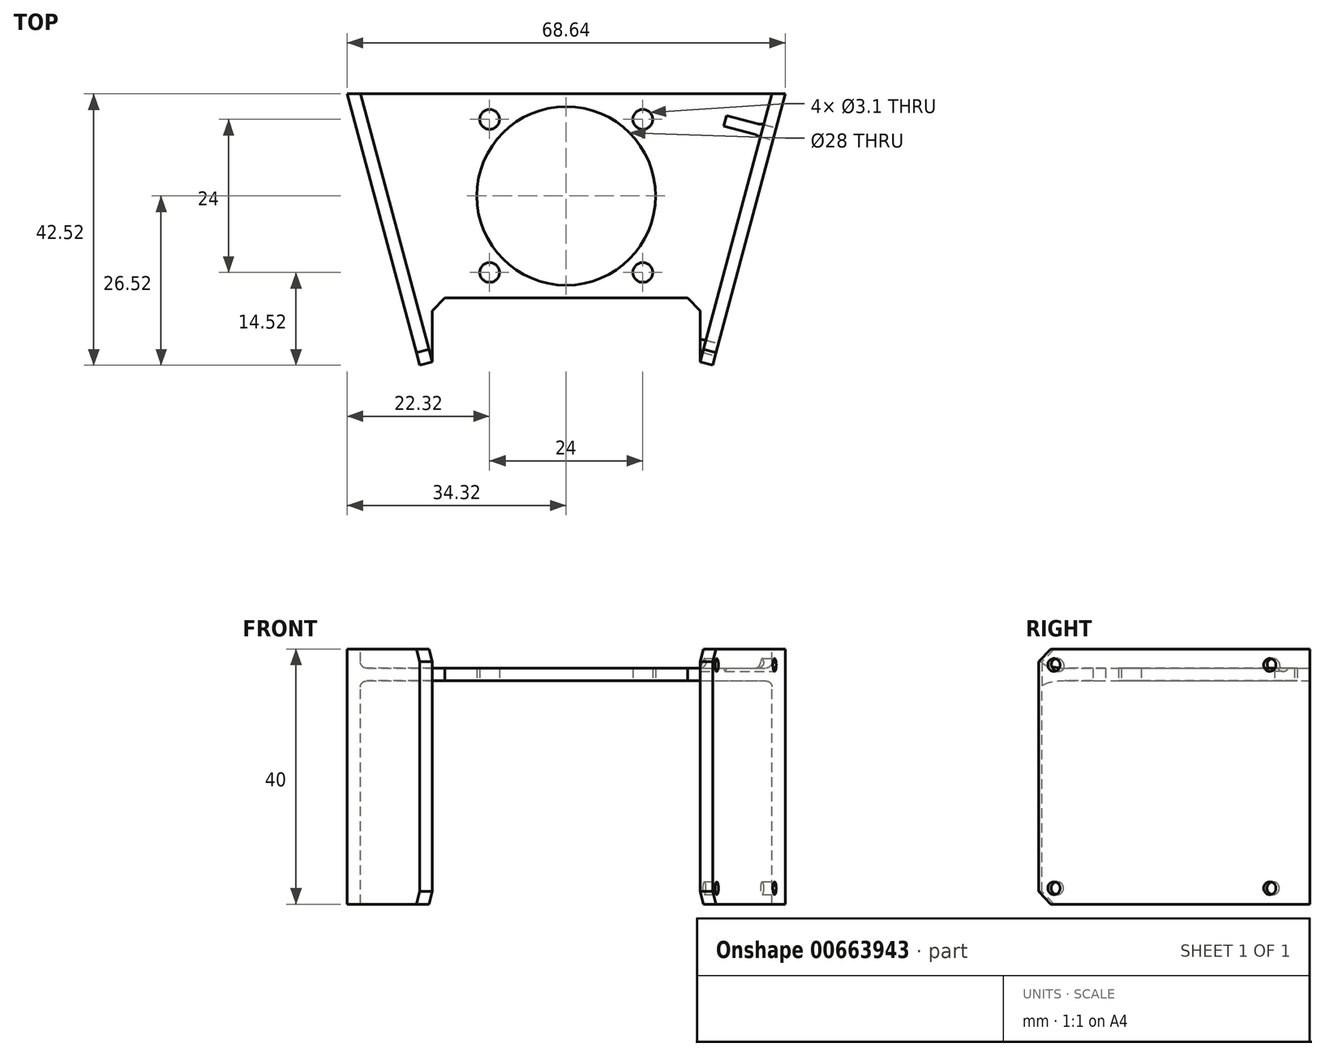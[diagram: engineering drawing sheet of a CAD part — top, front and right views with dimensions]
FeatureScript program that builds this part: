
annotation { "Feature Type Name" : "Feature", "Feature Type Description" : "" }
export const myFeature = defineFeature(function(context is Context, id is Id, definition is map)
    precondition{}
    {
        {
            var Q0;
            Q0=qCreatedBy(makeId("Top.planeOp"),FACE);
            var sketch = newSketch(context, id + "F0", { "sketchPlane" : qUnion([Q0])});
            skLineSegment(sketch, "E0.bottom", {"start": v(-16, 16) * mm, "end": v(16, 16) * mm});
            skLineSegment(sketch, "E0.top", {"start": v(-16, -16) * mm, "end": v(16, -16) * mm});
            skLineSegment(sketch, "E0.left", {"start": v(-16, 16) * mm, "end": v(-16, -16) * mm});
            skLineSegment(sketch, "E0.right", {"start": v(16, 16) * mm, "end": v(16, -16) * mm});
            skPoint(sketch, "E1.end.orphan", {"position": v(-27.25, 16) * mm});
            skPoint(sketch, "E2.end.orphan", {"position": v(-16, -26) * mm});
            skLineSegment(sketch, "E3", {"start": v(-16, -16) * mm, "end": v(-21, -16) * mm});
            skLineSegment(sketch, "E4", {"start": v(-21, -16) * mm, "end": v(-21, -26) * mm});
            skLineSegment(sketch, "E5", {"start": v(-32.25, 16) * mm, "end": v(-16, 16) * mm});
            skLineSegment(sketch, "E6", {"start": v(-21, -26) * mm, "end": v(-22.93, -26.52) * mm});
            skLineSegment(sketch, "E7", {"start": v(-22.93, -26.52) * mm, "end": v(-34.19, 15.48) * mm});
            skLineSegment(sketch, "E8.MirrorCS", {"start": v(16, -16) * mm, "end": v(21, -16) * mm});
            skLineSegment(sketch, "E9.MirrorCS", {"start": v(21, -16) * mm, "end": v(21, -26) * mm});
            skLineSegment(sketch, "E10.MirrorCS", {"start": v(21, -26) * mm, "end": v(22.93, -26.52) * mm});
            skLineSegment(sketch, "E11.MirrorCS", {"start": v(22.93, -26.52) * mm, "end": v(34.19, 15.48) * mm});
            skLineSegment(sketch, "E12.MirrorCS", {"start": v(32.25, 16) * mm, "end": v(16, 16) * mm});
            skCircle(sketch, "E13", {"center": v(0, 0) * mm, "radius": 14 * mm});
            skCircle(sketch, "E14", {"center": v(-12, 12) * mm, "radius": 1.55 * mm});
            skCircle(sketch, "E15.0.1.0", {"center": v(-12, -12) * mm, "radius": 1.55 * mm});
            skCircle(sketch, "E15.1.0.0", {"center": v(12, 12) * mm, "radius": 1.55 * mm});
            skCircle(sketch, "E15.1.1.0", {"center": v(12, -12) * mm, "radius": 1.55 * mm});
            skLineSegment(sketch, "E15.direction1", {"start": v(-12, 12) * mm, "end": v(12, 12) * mm, "construction": true});
            skLineSegment(sketch, "E15.direction2", {"start": v(-12, 12) * mm, "end": v(-12, -12) * mm, "construction": true});
            skPoint(sketch, "E16.orphan", {"position": v(-34.32, 16) * mm});
            skPoint(sketch, "E17.MirrorCS.end.orphan", {"position": v(32.25, 16) * mm});
            skPoint(sketch, "E17.MirrorCS.start.orphan", {"position": v(34.32, 16) * mm});
            skLineSegment(sketch, "E18", {"start": v(-32.25, 16) * mm, "end": v(-34.32, 16) * mm});
            skLineSegment(sketch, "E19", {"start": v(-34.32, 16) * mm, "end": v(-34.19, 15.48) * mm});
            skLineSegment(sketch, "E20.MirrorCS", {"start": v(32.25, 16) * mm, "end": v(34.32, 16) * mm});
            skLineSegment(sketch, "E21.MirrorCS", {"start": v(34.32, 16) * mm, "end": v(34.19, 15.48) * mm});
            skSolve(sketch);
        }
        {
            var Q0;
            Q0 = qSketchRegion(id + "F0", true);
            extrude(context, id + "F1", {"entities" : qUnion([Q0]), "depth" : 2 * mm, "offsetDistance" : 25 * mm});
        }
        {
            var Q0;
            Q0=makeQuery(id+"F1.opExtrude","CAP_FACE",FACE,{"disambiguationData":[OSD([sQuery(id+"F0.wireOp",EDGE,"E0.bottom"),sQuery(id+"F0.wireOp",EDGE,"E0.top"),sQuery(id+"F0.wireOp",EDGE,"E3"),sQuery(id+"F0.wireOp",EDGE,"E4"),sQuery(id+"F0.wireOp",EDGE,"E5"),sQuery(id+"F0.wireOp",EDGE,"E6"),sQuery(id+"F0.wireOp",EDGE,"E7"),sQuery(id+"F0.wireOp",EDGE,"E8.MirrorCS"),sQuery(id+"F0.wireOp",EDGE,"E9.MirrorCS"),sQuery(id+"F0.wireOp",EDGE,"E10.MirrorCS"),sQuery(id+"F0.wireOp",EDGE,"E11.MirrorCS"),sQuery(id+"F0.wireOp",EDGE,"E12.MirrorCS"),sQuery(id+"F0.wireOp",EDGE,"E13"),sQuery(id+"F0.wireOp",EDGE,"E14"),sQuery(id+"F0.wireOp",EDGE,"E15.0.1.0"),sQuery(id+"F0.wireOp",EDGE,"E15.1.0.0"),sQuery(id+"F0.wireOp",EDGE,"E15.1.1.0"),sQuery(id+"F0.wireOp",EDGE,"g3s6btQA-WjSZ-mLAz-3Mlx-ke06xdscXXFO"),sQuery(id+"F0.wireOp",EDGE,"cd634426-3a8a-407d-a25f-cc673fb204210.MirrorCS")])],"isStart":true});
            var sketch = newSketch(context, id + "F2", { "sketchPlane" : qUnion([Q0])});
            skLineSegment(sketch, "E22", {"start": v(21, 26) * mm, "end": v(21, 26) * mm});
            skLineSegment(sketch, "E23", {"start": v(22.93, 26.52) * mm, "end": v(22.93, 26.52) * mm});
            skLineSegment(sketch, "E24.MirrorCS", {"start": v(-21, 26) * mm, "end": v(-21, 26) * mm});
            skLineSegment(sketch, "E25.MirrorCS", {"start": v(-22.93, 26.52) * mm, "end": v(-22.93, 26.52) * mm});
            skPoint(sketch, "E26.MirrorCS.end.orphan", {"position": v(-22.93, 26.52) * mm});
            skPoint(sketch, "E26.MirrorCS.start.orphan", {"position": v(-21, 26) * mm});
            skLineSegment(sketch, "E27", {"start": v(-22.93, 26.52) * mm, "end": v(-21, 26) * mm});
            skLineSegment(sketch, "E28", {"start": v(-22.93, 26.52) * mm, "end": v(-34.32, -16) * mm});
            skLineSegment(sketch, "E29", {"start": v(-34.32, -16) * mm, "end": v(-32.25, -16) * mm});
            skLineSegment(sketch, "E30", {"start": v(-21, 26) * mm, "end": v(-32.25, -16) * mm});
            skLineSegment(sketch, "E31.MirrorCS", {"start": v(21, 26) * mm, "end": v(32.25, -16) * mm});
            skLineSegment(sketch, "E32.MirrorCS", {"start": v(22.93, 26.52) * mm, "end": v(21, 26) * mm});
            skLineSegment(sketch, "E33.MirrorCS", {"start": v(22.93, 26.52) * mm, "end": v(34.32, -16) * mm});
            skLineSegment(sketch, "E34.MirrorCS", {"start": v(34.32, -16) * mm, "end": v(32.25, -16) * mm});
            skSolve(sketch);
        }
        {
            var Q0;
            Q0 = qSketchRegion(id + "F2", true);
            extrude(context, id + "F3", {"entities" : qUnion([Q0]), "operationType" : NewBodyOperationType.ADD, "depth" : 35 * mm, "offsetDistance" : 25 * mm, "hasSecondDirection" : true, "secondDirectionOppositeDirection" : true, "secondDirectionDepth" : 5 * mm});
        }
        {
            var Q0;
            Q0=makeQuery(id+"F3.boolean.opBoolean","MERGE",FACE,{"derivedFrom":[makeQuery(id+"F1.opExtrude","SWEPT_FACE",FACE,{"disambiguationData":[OSD([sQuery(id+"F0.wireOp",EDGE,"E11.MirrorCS"),sQuery(id+"F0.wireOp",EDGE,"E21.MirrorCS")])]}),makeQuery(id+"F3.opExtrude","SWEPT_FACE",FACE,{"disambiguationData":[OSD([sQuery(id+"F2.wireOp",EDGE,"E33.MirrorCS")])]})]});
            var sketch = newSketch(context, id + "F4", { "sketchPlane" : qUnion([Q0])});
            skCircle(sketch, "E35", {"center": v(-17.18, 2.5) * mm, "radius": 1 * mm});
            skCircle(sketch, "E36.0.1.0", {"center": v(-17.18, -32.5) * mm, "radius": 1 * mm});
            skCircle(sketch, "E36.1.0.0", {"center": v(17.82, 2.5) * mm, "radius": 1 * mm});
            skCircle(sketch, "E36.1.1.0", {"center": v(17.82, -32.5) * mm, "radius": 1 * mm});
            skLineSegment(sketch, "E36.direction1", {"start": v(-17.18, 2.5) * mm, "end": v(17.82, 2.5) * mm, "construction": true});
            skLineSegment(sketch, "E36.direction2", {"start": v(-17.18, 2.5) * mm, "end": v(-17.18, -32.5) * mm, "construction": true});
            skSolve(sketch);
        }
        {
            var Q0;
            Q0 = qSketchRegion(id + "F4", true);
            extrude(context, id + "F5", {"entities" : qUnion([Q0]), "operationType" : NewBodyOperationType.REMOVE, "oppositeDirection" : true, "depth" : 8 * mm, "offsetDistance" : 25 * mm});
        }
        {
            var Q0;
            Q0=makeQuery(id+"F3.opExtrude","CAP_EDGE",EDGE,{"disambiguationData":[OSD([sQuery(id+"F2.wireOp",EDGE,"E32.MirrorCS")])],"isStart":false});
            var Q1;
            Q1=makeQuery(id+"F3.opExtrude","CAP_EDGE",EDGE,{"disambiguationData":[OSD([sQuery(id+"F2.wireOp",EDGE,"E32.MirrorCS")])],"isStart":true});
            var Q2;
            Q2=makeQuery(id+"F3.opExtrude","CAP_EDGE",EDGE,{"disambiguationData":[OSD([sQuery(id+"F2.wireOp",EDGE,"E27")])],"isStart":true});
            var Q3;
            Q3=makeQuery(id+"F3.opExtrude","CAP_EDGE",EDGE,{"disambiguationData":[OSD([sQuery(id+"F2.wireOp",EDGE,"E27")])],"isStart":false});
            var Q4;
            Q4=makeQuery(id+"F1.opExtrude","SWEPT_EDGE",EDGE,{"disambiguationData":[OSD([sQuery(id+"F0.wireOp",EDGE,"E3"),sQuery(id+"F0.wireOp",EDGE,"E4")])]});
            var Q5;
            Q5=makeQuery(id+"F1.opExtrude","SWEPT_EDGE",EDGE,{"disambiguationData":[OSD([sQuery(id+"F0.wireOp",EDGE,"E8.MirrorCS"),sQuery(id+"F0.wireOp",EDGE,"E9.MirrorCS")])]});
            chamfer(context, id + "F6", {"entities" : qUnion([Q0, Q1, Q2, Q3, Q4, Q5]), "width" : 2 * mm, "tangentPropagation" : true});
        }
        {
            var Q0;
            {var subQ0=makeQuery(id+"F1.opExtrude","CAP_FACE",FACE,{"disambiguationData":[OSD([sQuery(id+"F0.wireOp",EDGE,"E0.bottom"),sQuery(id+"F0.wireOp",EDGE,"E0.top"),sQuery(id+"F0.wireOp",EDGE,"E3"),sQuery(id+"F0.wireOp",EDGE,"E4"),sQuery(id+"F0.wireOp",EDGE,"E5"),sQuery(id+"F0.wireOp",EDGE,"E6"),sQuery(id+"F0.wireOp",EDGE,"E7"),sQuery(id+"F0.wireOp",EDGE,"E8.MirrorCS"),sQuery(id+"F0.wireOp",EDGE,"E9.MirrorCS"),sQuery(id+"F0.wireOp",EDGE,"E10.MirrorCS"),sQuery(id+"F0.wireOp",EDGE,"E11.MirrorCS"),sQuery(id+"F0.wireOp",EDGE,"E12.MirrorCS"),sQuery(id+"F0.wireOp",EDGE,"E13"),sQuery(id+"F0.wireOp",EDGE,"E14"),sQuery(id+"F0.wireOp",EDGE,"E15.0.1.0"),sQuery(id+"F0.wireOp",EDGE,"E15.1.0.0"),sQuery(id+"F0.wireOp",EDGE,"E15.1.1.0"),sQuery(id+"F0.wireOp",EDGE,"E18"),sQuery(id+"F0.wireOp",EDGE,"E19"),sQuery(id+"F0.wireOp",EDGE,"E20.MirrorCS"),sQuery(id+"F0.wireOp",EDGE,"E21.MirrorCS")])],"isStart":false});var subQ1=makeQuery(id+"F3.opExtrude","SWEPT_FACE",FACE,{"disambiguationData":[OSD([sQuery(id+"F2.wireOp",EDGE,"E31.MirrorCS")])]});Q0=makeQuery(id+"F5.boolean.opBoolean","SPLIT",EDGE,{"disambiguationData":[TD([subQ0,subQ1,makeQuery(id+"F5.opExtrude","SWEPT_FACE",FACE,{"disambiguationData":[OSD([sQuery(id+"F4.wireOp",EDGE,"E35")])]}),makeQuery(id+"F5.opExtrude","SWEPT_FACE",FACE,{"disambiguationData":[OSD([sQuery(id+"F4.wireOp",EDGE,"E36.1.0.0")])]})])],"derivedFrom":makeQuery(id+"F3.boolean.opBoolean","INTERSECT",EDGE,{"derivedFrom":[subQ0,subQ1]})});}
            var Q1;
            {var subQ0=makeQuery(id+"F3.opExtrude","SWEPT_FACE",FACE,{"disambiguationData":[OSD([sQuery(id+"F2.wireOp",EDGE,"E31.MirrorCS")])]});var subQ1=sQuery(id+"F0.wireOp",EDGE,"E20.MirrorCS");var subQ2=sQuery(id+"F0.wireOp",EDGE,"E18");var subQ3=sQuery(id+"F0.wireOp",EDGE,"E12.MirrorCS");var subQ4=sQuery(id+"F0.wireOp",EDGE,"E5");var subQ5=sQuery(id+"F0.wireOp",EDGE,"E0.bottom");var subQ6=makeQuery(id+"F1.opExtrude","CAP_FACE",FACE,{"disambiguationData":[OSD([subQ5,sQuery(id+"F0.wireOp",EDGE,"E0.top"),sQuery(id+"F0.wireOp",EDGE,"E3"),sQuery(id+"F0.wireOp",EDGE,"E4"),subQ4,sQuery(id+"F0.wireOp",EDGE,"E6"),sQuery(id+"F0.wireOp",EDGE,"E7"),sQuery(id+"F0.wireOp",EDGE,"E8.MirrorCS"),sQuery(id+"F0.wireOp",EDGE,"E9.MirrorCS"),sQuery(id+"F0.wireOp",EDGE,"E10.MirrorCS"),sQuery(id+"F0.wireOp",EDGE,"E11.MirrorCS"),subQ3,sQuery(id+"F0.wireOp",EDGE,"E13"),sQuery(id+"F0.wireOp",EDGE,"E14"),sQuery(id+"F0.wireOp",EDGE,"E15.0.1.0"),sQuery(id+"F0.wireOp",EDGE,"E15.1.0.0"),sQuery(id+"F0.wireOp",EDGE,"E15.1.1.0"),subQ2,sQuery(id+"F0.wireOp",EDGE,"E19"),subQ1,sQuery(id+"F0.wireOp",EDGE,"E21.MirrorCS")])],"isStart":false});Q1=makeQuery(id+"F5.boolean.opBoolean","SPLIT",EDGE,{"disambiguationData":[TD([subQ6,makeQuery(id+"F1.opExtrude","SWEPT_FACE",FACE,{"disambiguationData":[OSD([subQ5,subQ4,subQ3,subQ2,subQ1])]}),makeQuery(id+"F3.opExtrude","SWEPT_FACE",FACE,{"disambiguationData":[OSD([sQuery(id+"F2.wireOp",EDGE,"E29")])]}),subQ0,makeQuery(id+"F3.opExtrude","SWEPT_FACE",FACE,{"disambiguationData":[OSD([sQuery(id+"F2.wireOp",EDGE,"E34.MirrorCS")])]}),makeQuery(id+"F5.opExtrude","SWEPT_FACE",FACE,{"disambiguationData":[OSD([sQuery(id+"F4.wireOp",EDGE,"E36.1.0.0")])]})])],"derivedFrom":makeQuery(id+"F3.boolean.opBoolean","INTERSECT",EDGE,{"derivedFrom":[subQ6,subQ0]})});}
            var Q2;
            {var subQ0=makeQuery(id+"F3.opExtrude","SWEPT_FACE",FACE,{"disambiguationData":[OSD([sQuery(id+"F2.wireOp",EDGE,"E31.MirrorCS")])]});var subQ1=sQuery(id+"F0.wireOp",EDGE,"E9.MirrorCS");var subQ2=sQuery(id+"F0.wireOp",EDGE,"E10.MirrorCS");var subQ3=makeQuery(id+"F1.opExtrude","CAP_FACE",FACE,{"disambiguationData":[OSD([sQuery(id+"F0.wireOp",EDGE,"E0.bottom"),sQuery(id+"F0.wireOp",EDGE,"E0.top"),sQuery(id+"F0.wireOp",EDGE,"E3"),sQuery(id+"F0.wireOp",EDGE,"E4"),sQuery(id+"F0.wireOp",EDGE,"E5"),sQuery(id+"F0.wireOp",EDGE,"E6"),sQuery(id+"F0.wireOp",EDGE,"E7"),sQuery(id+"F0.wireOp",EDGE,"E8.MirrorCS"),subQ1,subQ2,sQuery(id+"F0.wireOp",EDGE,"E11.MirrorCS"),sQuery(id+"F0.wireOp",EDGE,"E12.MirrorCS"),sQuery(id+"F0.wireOp",EDGE,"E13"),sQuery(id+"F0.wireOp",EDGE,"E14"),sQuery(id+"F0.wireOp",EDGE,"E15.0.1.0"),sQuery(id+"F0.wireOp",EDGE,"E15.1.0.0"),sQuery(id+"F0.wireOp",EDGE,"E15.1.1.0"),sQuery(id+"F0.wireOp",EDGE,"E18"),sQuery(id+"F0.wireOp",EDGE,"E19"),sQuery(id+"F0.wireOp",EDGE,"E20.MirrorCS"),sQuery(id+"F0.wireOp",EDGE,"E21.MirrorCS")])],"isStart":false});Q2=makeQuery(id+"F5.boolean.opBoolean","SPLIT",EDGE,{"disambiguationData":[TD([subQ3,makeQuery(id+"F1.opExtrude","SWEPT_FACE",FACE,{"disambiguationData":[OSD([subQ1])]}),makeQuery(id+"F1.opExtrude","SWEPT_FACE",FACE,{"disambiguationData":[OSD([subQ2])]}),subQ0,makeQuery(id+"F3.opExtrude","SWEPT_FACE",FACE,{"disambiguationData":[OSD([sQuery(id+"F2.wireOp",EDGE,"E32.MirrorCS")])]}),makeQuery(id+"F5.opExtrude","SWEPT_FACE",FACE,{"disambiguationData":[OSD([sQuery(id+"F4.wireOp",EDGE,"E35")])]})])],"derivedFrom":makeQuery(id+"F3.boolean.opBoolean","INTERSECT",EDGE,{"derivedFrom":[subQ3,subQ0]})});}
            var Q3;
            {var subQ0=sQuery(id+"F0.wireOp",EDGE,"E6");var subQ1=sQuery(id+"F0.wireOp",EDGE,"E4");var subQ2=makeQuery(id+"F1.opExtrude","CAP_FACE",FACE,{"disambiguationData":[OSD([sQuery(id+"F0.wireOp",EDGE,"E0.bottom"),sQuery(id+"F0.wireOp",EDGE,"E0.top"),sQuery(id+"F0.wireOp",EDGE,"E3"),subQ1,sQuery(id+"F0.wireOp",EDGE,"E5"),subQ0,sQuery(id+"F0.wireOp",EDGE,"E7"),sQuery(id+"F0.wireOp",EDGE,"E8.MirrorCS"),sQuery(id+"F0.wireOp",EDGE,"E9.MirrorCS"),sQuery(id+"F0.wireOp",EDGE,"E10.MirrorCS"),sQuery(id+"F0.wireOp",EDGE,"E11.MirrorCS"),sQuery(id+"F0.wireOp",EDGE,"E12.MirrorCS"),sQuery(id+"F0.wireOp",EDGE,"E13"),sQuery(id+"F0.wireOp",EDGE,"E14"),sQuery(id+"F0.wireOp",EDGE,"E15.0.1.0"),sQuery(id+"F0.wireOp",EDGE,"E15.1.0.0"),sQuery(id+"F0.wireOp",EDGE,"E15.1.1.0"),sQuery(id+"F0.wireOp",EDGE,"E18"),sQuery(id+"F0.wireOp",EDGE,"E19"),sQuery(id+"F0.wireOp",EDGE,"E20.MirrorCS"),sQuery(id+"F0.wireOp",EDGE,"E21.MirrorCS")])],"isStart":false});var subQ3=makeQuery(id+"F3.opExtrude","SWEPT_FACE",FACE,{"disambiguationData":[OSD([sQuery(id+"F2.wireOp",EDGE,"E30")])]});Q3=makeQuery(id+"FOjCWlT8B3Rebb0_1.1.F5.boolean.opBoolean","SPLIT",EDGE,{"disambiguationData":[TD([subQ2,makeQuery(id+"F1.opExtrude","SWEPT_FACE",FACE,{"disambiguationData":[OSD([subQ1])]}),makeQuery(id+"F1.opExtrude","SWEPT_FACE",FACE,{"disambiguationData":[OSD([subQ0])]}),makeQuery(id+"F3.opExtrude","SWEPT_FACE",FACE,{"disambiguationData":[OSD([sQuery(id+"F2.wireOp",EDGE,"E27")])]}),subQ3,makeQuery(id+"FOjCWlT8B3Rebb0_1.1.F5.opExtrude","SWEPT_FACE",FACE,{"disambiguationData":[OSD([sQuery(id+"F4.wireOp",EDGE,"E35")])]})])],"derivedFrom":makeQuery(id+"F3.boolean.opBoolean","INTERSECT",EDGE,{"derivedFrom":[subQ2,subQ3]})});}
            var Q4;
            {var subQ0=makeQuery(id+"F1.opExtrude","CAP_FACE",FACE,{"disambiguationData":[OSD([sQuery(id+"F0.wireOp",EDGE,"E0.bottom"),sQuery(id+"F0.wireOp",EDGE,"E0.top"),sQuery(id+"F0.wireOp",EDGE,"E3"),sQuery(id+"F0.wireOp",EDGE,"E4"),sQuery(id+"F0.wireOp",EDGE,"E5"),sQuery(id+"F0.wireOp",EDGE,"E6"),sQuery(id+"F0.wireOp",EDGE,"E7"),sQuery(id+"F0.wireOp",EDGE,"E8.MirrorCS"),sQuery(id+"F0.wireOp",EDGE,"E9.MirrorCS"),sQuery(id+"F0.wireOp",EDGE,"E10.MirrorCS"),sQuery(id+"F0.wireOp",EDGE,"E11.MirrorCS"),sQuery(id+"F0.wireOp",EDGE,"E12.MirrorCS"),sQuery(id+"F0.wireOp",EDGE,"E13"),sQuery(id+"F0.wireOp",EDGE,"E14"),sQuery(id+"F0.wireOp",EDGE,"E15.0.1.0"),sQuery(id+"F0.wireOp",EDGE,"E15.1.0.0"),sQuery(id+"F0.wireOp",EDGE,"E15.1.1.0"),sQuery(id+"F0.wireOp",EDGE,"E18"),sQuery(id+"F0.wireOp",EDGE,"E19"),sQuery(id+"F0.wireOp",EDGE,"E20.MirrorCS"),sQuery(id+"F0.wireOp",EDGE,"E21.MirrorCS")])],"isStart":false});var subQ1=makeQuery(id+"F3.opExtrude","SWEPT_FACE",FACE,{"disambiguationData":[OSD([sQuery(id+"F2.wireOp",EDGE,"E30")])]});Q4=makeQuery(id+"FOjCWlT8B3Rebb0_1.1.F5.boolean.opBoolean","SPLIT",EDGE,{"disambiguationData":[TD([subQ0,subQ1,makeQuery(id+"FOjCWlT8B3Rebb0_1.1.F5.opExtrude","SWEPT_FACE",FACE,{"disambiguationData":[OSD([sQuery(id+"F4.wireOp",EDGE,"E35")])]}),makeQuery(id+"FOjCWlT8B3Rebb0_1.1.F5.opExtrude","SWEPT_FACE",FACE,{"disambiguationData":[OSD([sQuery(id+"F4.wireOp",EDGE,"E36.1.0.0")])]})])],"derivedFrom":makeQuery(id+"F3.boolean.opBoolean","INTERSECT",EDGE,{"derivedFrom":[subQ0,subQ1]})});}
            var Q5;
            {var subQ0=makeQuery(id+"F3.opExtrude","SWEPT_FACE",FACE,{"disambiguationData":[OSD([sQuery(id+"F2.wireOp",EDGE,"E30")])]});var subQ1=sQuery(id+"F0.wireOp",EDGE,"E20.MirrorCS");var subQ2=sQuery(id+"F0.wireOp",EDGE,"E18");var subQ3=sQuery(id+"F0.wireOp",EDGE,"E12.MirrorCS");var subQ4=sQuery(id+"F0.wireOp",EDGE,"E5");var subQ5=sQuery(id+"F0.wireOp",EDGE,"E0.bottom");var subQ6=makeQuery(id+"F1.opExtrude","CAP_FACE",FACE,{"disambiguationData":[OSD([subQ5,sQuery(id+"F0.wireOp",EDGE,"E0.top"),sQuery(id+"F0.wireOp",EDGE,"E3"),sQuery(id+"F0.wireOp",EDGE,"E4"),subQ4,sQuery(id+"F0.wireOp",EDGE,"E6"),sQuery(id+"F0.wireOp",EDGE,"E7"),sQuery(id+"F0.wireOp",EDGE,"E8.MirrorCS"),sQuery(id+"F0.wireOp",EDGE,"E9.MirrorCS"),sQuery(id+"F0.wireOp",EDGE,"E10.MirrorCS"),sQuery(id+"F0.wireOp",EDGE,"E11.MirrorCS"),subQ3,sQuery(id+"F0.wireOp",EDGE,"E13"),sQuery(id+"F0.wireOp",EDGE,"E14"),sQuery(id+"F0.wireOp",EDGE,"E15.0.1.0"),sQuery(id+"F0.wireOp",EDGE,"E15.1.0.0"),sQuery(id+"F0.wireOp",EDGE,"E15.1.1.0"),subQ2,sQuery(id+"F0.wireOp",EDGE,"E19"),subQ1,sQuery(id+"F0.wireOp",EDGE,"E21.MirrorCS")])],"isStart":false});Q5=makeQuery(id+"FOjCWlT8B3Rebb0_1.1.F5.boolean.opBoolean","SPLIT",EDGE,{"disambiguationData":[TD([subQ6,makeQuery(id+"F1.opExtrude","SWEPT_FACE",FACE,{"disambiguationData":[OSD([subQ5,subQ4,subQ3,subQ2,subQ1])]}),makeQuery(id+"F3.opExtrude","SWEPT_FACE",FACE,{"disambiguationData":[OSD([sQuery(id+"F2.wireOp",EDGE,"E29")])]}),subQ0,makeQuery(id+"F3.opExtrude","SWEPT_FACE",FACE,{"disambiguationData":[OSD([sQuery(id+"F2.wireOp",EDGE,"E34.MirrorCS")])]}),makeQuery(id+"FOjCWlT8B3Rebb0_1.1.F5.opExtrude","SWEPT_FACE",FACE,{"disambiguationData":[OSD([sQuery(id+"F4.wireOp",EDGE,"E36.1.0.0")])]})])],"derivedFrom":makeQuery(id+"F3.boolean.opBoolean","INTERSECT",EDGE,{"derivedFrom":[subQ6,subQ0]})});}
            var Q6;
            Q6=makeQuery(id+"F3.boolean.opBoolean","INTERSECT",EDGE,{"derivedFrom":[makeQuery(id+"F1.opExtrude","CAP_FACE",FACE,{"disambiguationData":[OSD([sQuery(id+"F0.wireOp",EDGE,"E0.bottom"),sQuery(id+"F0.wireOp",EDGE,"E0.top"),sQuery(id+"F0.wireOp",EDGE,"E3"),sQuery(id+"F0.wireOp",EDGE,"E4"),sQuery(id+"F0.wireOp",EDGE,"E5"),sQuery(id+"F0.wireOp",EDGE,"E6"),sQuery(id+"F0.wireOp",EDGE,"E7"),sQuery(id+"F0.wireOp",EDGE,"E8.MirrorCS"),sQuery(id+"F0.wireOp",EDGE,"E9.MirrorCS"),sQuery(id+"F0.wireOp",EDGE,"E10.MirrorCS"),sQuery(id+"F0.wireOp",EDGE,"E11.MirrorCS"),sQuery(id+"F0.wireOp",EDGE,"E12.MirrorCS"),sQuery(id+"F0.wireOp",EDGE,"E13"),sQuery(id+"F0.wireOp",EDGE,"E14"),sQuery(id+"F0.wireOp",EDGE,"E15.0.1.0"),sQuery(id+"F0.wireOp",EDGE,"E15.1.0.0"),sQuery(id+"F0.wireOp",EDGE,"E15.1.1.0"),sQuery(id+"F0.wireOp",EDGE,"E18"),sQuery(id+"F0.wireOp",EDGE,"E19"),sQuery(id+"F0.wireOp",EDGE,"E20.MirrorCS"),sQuery(id+"F0.wireOp",EDGE,"E21.MirrorCS")])],"isStart":true}),makeQuery(id+"F3.opExtrude","SWEPT_FACE",FACE,{"disambiguationData":[OSD([sQuery(id+"F2.wireOp",EDGE,"E30")])]})]});
            var Q7;
            Q7=makeQuery(id+"F3.boolean.opBoolean","INTERSECT",EDGE,{"derivedFrom":[makeQuery(id+"F1.opExtrude","CAP_FACE",FACE,{"disambiguationData":[OSD([sQuery(id+"F0.wireOp",EDGE,"E0.bottom"),sQuery(id+"F0.wireOp",EDGE,"E0.top"),sQuery(id+"F0.wireOp",EDGE,"E3"),sQuery(id+"F0.wireOp",EDGE,"E4"),sQuery(id+"F0.wireOp",EDGE,"E5"),sQuery(id+"F0.wireOp",EDGE,"E6"),sQuery(id+"F0.wireOp",EDGE,"E7"),sQuery(id+"F0.wireOp",EDGE,"E8.MirrorCS"),sQuery(id+"F0.wireOp",EDGE,"E9.MirrorCS"),sQuery(id+"F0.wireOp",EDGE,"E10.MirrorCS"),sQuery(id+"F0.wireOp",EDGE,"E11.MirrorCS"),sQuery(id+"F0.wireOp",EDGE,"E12.MirrorCS"),sQuery(id+"F0.wireOp",EDGE,"E13"),sQuery(id+"F0.wireOp",EDGE,"E14"),sQuery(id+"F0.wireOp",EDGE,"E15.0.1.0"),sQuery(id+"F0.wireOp",EDGE,"E15.1.0.0"),sQuery(id+"F0.wireOp",EDGE,"E15.1.1.0"),sQuery(id+"F0.wireOp",EDGE,"E18"),sQuery(id+"F0.wireOp",EDGE,"E19"),sQuery(id+"F0.wireOp",EDGE,"E20.MirrorCS"),sQuery(id+"F0.wireOp",EDGE,"E21.MirrorCS")])],"isStart":true}),makeQuery(id+"F3.opExtrude","SWEPT_FACE",FACE,{"disambiguationData":[OSD([sQuery(id+"F2.wireOp",EDGE,"E31.MirrorCS")])]})]});
            fillet(context, id + "F7", {"entities" : qUnion([Q0, Q1, Q2, Q3, Q4, Q5, Q6, Q7]), "radius" : 1 * mm, "tangentPropagation" : true, "allowEdgeOverflow" : false});
        }
    });
